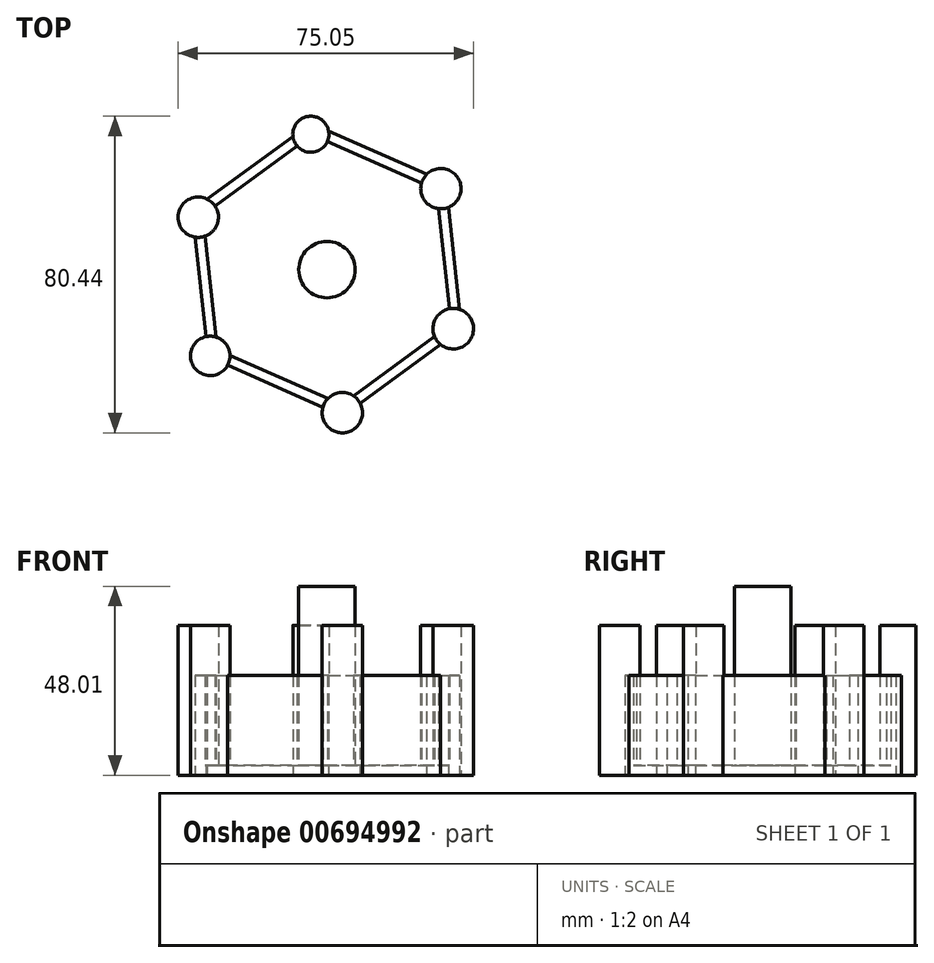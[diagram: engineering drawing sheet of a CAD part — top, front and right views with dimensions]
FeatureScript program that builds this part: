
annotation { "Feature Type Name" : "Feature", "Feature Type Description" : "" }
export const myFeature = defineFeature(function(context is Context, id is Id, definition is map)
    precondition{}
    {
        {
            var Q0;
            Q0=qCreatedBy(makeId("Top.planeOp"),FACE);
            var sketch = newSketch(context, id + "F0", { "sketchPlane" : qUnion([Q0])});
            skCircle(sketch, "E0.cCircle", {"center": v(0, 0) * mm, "radius": 32.4 * mm, "construction": true});
            skLineSegment(sketch, "E0.0", {"start": v(34.23, -15.11) * mm, "end": v(4.03, -37.2) * mm});
            skLineSegment(sketch, "E0.1", {"start": v(4.03, -37.2) * mm, "end": v(-30.2, -22.1) * mm});
            skLineSegment(sketch, "E0.2", {"start": v(-30.2, -22.1) * mm, "end": v(-34.23, 15.11) * mm});
            skLineSegment(sketch, "E0.3", {"start": v(-34.23, 15.11) * mm, "end": v(-4.03, 37.2) * mm});
            skLineSegment(sketch, "E0.4", {"start": v(-4.03, 37.2) * mm, "end": v(30.2, 22.1) * mm});
            skLineSegment(sketch, "E0.5", {"start": v(30.2, 22.1) * mm, "end": v(34.23, -15.11) * mm});
            skPoint(sketch, "E0.0.midPoint", {"position": v(19.13, -26.16) * mm});
            skSolve(sketch);
        }
        {
            var Q0;
            Q0=makeQuery(id+"F0.imprint","IMPRINT",FACE,{"disambiguationData":[TD([[makeQuery(id+"F0.imprint","IMPRINT",EDGE,{"derivedFrom":sQuery(id+"F0.wireOp",EDGE,"E0.0")}),-1.0]])]});
            extrude(context, id + "F1", {"entities" : qUnion([Q0]), "depth" : 25.4 * mm, "offsetDistance" : 25.4 * mm});
        }
        {
            var Q0;
            Q0=makeQuery(id+"F1.opExtrude","CAP_FACE",FACE,{"disambiguationData":[OSD([sQuery(id+"F0.wireOp",EDGE,"E0.0"),sQuery(id+"F0.wireOp",EDGE,"E0.1"),sQuery(id+"F0.wireOp",EDGE,"E0.2"),sQuery(id+"F0.wireOp",EDGE,"E0.3"),sQuery(id+"F0.wireOp",EDGE,"E0.4"),sQuery(id+"F0.wireOp",EDGE,"E0.5")])],"isStart":false});
            shell(context, id + "F2", {"entities" : qUnion([Q0]), "thickness" : 2.54 * mm});
        }
        {
            var Q0;
            Q0=qCreatedBy(makeId("Top.planeOp"),FACE);
            var sketch = newSketch(context, id + "F3", { "sketchPlane" : qUnion([Q0])});
            skCircle(sketch, "E1", {"center": v(0, 0) * mm, "radius": 7.16 * mm});
            skSolve(sketch);
        }
        {
            var Q0;
            Q0=makeQuery(id+"F3.imprint","IMPRINT",FACE,{"disambiguationData":[TD([[makeQuery(id+"F3.imprint","IMPRINT",EDGE,{"derivedFrom":sQuery(id+"F3.wireOp",EDGE,"E1")}),1.0]])]});
            extrude(context, id + "F4", {"entities" : qUnion([Q0]), "operationType" : NewBodyOperationType.ADD, "depth" : 48 * mm, "offsetDistance" : 25.4 * mm});
        }
        {
            var Q0;
            Q0=qCreatedBy(makeId("Top.planeOp"),FACE);
            var sketch = newSketch(context, id + "F5", { "sketchPlane" : qUnion([Q0])});
            skCircle(sketch, "E2", {"center": v(28.95, 20.6) * mm, "radius": 5.12 * mm});
            skSolve(sketch);
        }
        {
            var Q0;
            Q0=qCreatedBy(makeId("Top.planeOp"),FACE);
            var sketch = newSketch(context, id + "F6", { "sketchPlane" : qUnion([Q0])});
            skCircle(sketch, "E3", {"center": v(-29.66, -21.9) * mm, "radius": 5 * mm});
            skSolve(sketch);
        }
        {
            var Q0;
            Q0=qCreatedBy(makeId("Top.planeOp"),FACE);
            var sketch = newSketch(context, id + "F7", { "sketchPlane" : qUnion([Q0])});
            skCircle(sketch, "E4", {"center": v(-32.7, 13.33) * mm, "radius": 5.12 * mm});
            skSolve(sketch);
        }
        {
            var Q0;
            Q0=qCreatedBy(makeId("Top.planeOp"),FACE);
            var sketch = newSketch(context, id + "F8", { "sketchPlane" : qUnion([Q0])});
            skCircle(sketch, "E5", {"center": v(-4.1, 34.4) * mm, "radius": 4.59 * mm});
            skSolve(sketch);
        }
        {
            var Q0;
            Q0=qCreatedBy(makeId("Top.planeOp"),FACE);
            var sketch = newSketch(context, id + "F9", { "sketchPlane" : qUnion([Q0])});
            skCircle(sketch, "E6", {"center": v(32.07, -14.99) * mm, "radius": 5.16 * mm});
            skSolve(sketch);
        }
        {
            var Q0;
            Q0=qCreatedBy(makeId("Top.planeOp"),FACE);
            var sketch = newSketch(context, id + "F10", { "sketchPlane" : qUnion([Q0])});
            skCircle(sketch, "E7", {"center": v(3.9, -36.33) * mm, "radius": 5.12 * mm});
            skSolve(sketch);
        }
        {
            var Q0;
            Q0=makeQuery(id+"F5.imprint","IMPRINT",FACE,{"disambiguationData":[TD([[makeQuery(id+"F5.imprint","IMPRINT",EDGE,{"derivedFrom":sQuery(id+"F5.wireOp",EDGE,"E2")}),1.0]])]});
            extrude(context, id + "F11", {"entities" : qUnion([Q0]), "operationType" : NewBodyOperationType.ADD, "depth" : 38.1 * mm, "offsetDistance" : 25.4 * mm});
        }
        {
            var Q0;
            Q0=makeQuery(id+"F10.imprint","IMPRINT",FACE,{"disambiguationData":[TD([[makeQuery(id+"F10.imprint","IMPRINT",EDGE,{"derivedFrom":sQuery(id+"F10.wireOp",EDGE,"E7")}),1.0]])]});
            extrude(context, id + "F12", {"entities" : qUnion([Q0]), "operationType" : NewBodyOperationType.ADD, "depth" : 38.1 * mm, "offsetDistance" : 25.4 * mm});
        }
        {
            var Q0;
            Q0=makeQuery(id+"F9.imprint","IMPRINT",FACE,{"disambiguationData":[TD([[makeQuery(id+"F9.imprint","IMPRINT",EDGE,{"derivedFrom":sQuery(id+"F9.wireOp",EDGE,"E6")}),1.0]])]});
            extrude(context, id + "F13", {"entities" : qUnion([Q0]), "operationType" : NewBodyOperationType.ADD, "depth" : 38.1 * mm, "offsetDistance" : 25.4 * mm});
        }
        {
            var Q0;
            Q0=makeQuery(id+"F7.imprint","IMPRINT",FACE,{"disambiguationData":[TD([[makeQuery(id+"F7.imprint","IMPRINT",EDGE,{"derivedFrom":sQuery(id+"F7.wireOp",EDGE,"E4")}),1.0]])]});
            extrude(context, id + "F14", {"entities" : qUnion([Q0]), "operationType" : NewBodyOperationType.ADD, "depth" : 38.1 * mm, "offsetDistance" : 25.4 * mm});
        }
        {
            var Q0;
            Q0=makeQuery(id+"F6.imprint","IMPRINT",FACE,{"disambiguationData":[TD([[makeQuery(id+"F6.imprint","IMPRINT",EDGE,{"derivedFrom":sQuery(id+"F6.wireOp",EDGE,"E3")}),1.0]])]});
            extrude(context, id + "F15", {"entities" : qUnion([Q0]), "operationType" : NewBodyOperationType.ADD, "depth" : 38.1 * mm, "offsetDistance" : 25.4 * mm});
        }
        {
            var Q0;
            Q0=makeQuery(id+"F8.imprint","IMPRINT",FACE,{"disambiguationData":[TD([[makeQuery(id+"F8.imprint","IMPRINT",EDGE,{"derivedFrom":sQuery(id+"F8.wireOp",EDGE,"E5")}),1.0]])]});
            extrude(context, id + "F16", {"entities" : qUnion([Q0]), "operationType" : NewBodyOperationType.ADD, "depth" : 38.1 * mm, "offsetDistance" : 25.4 * mm});
        }
    });
